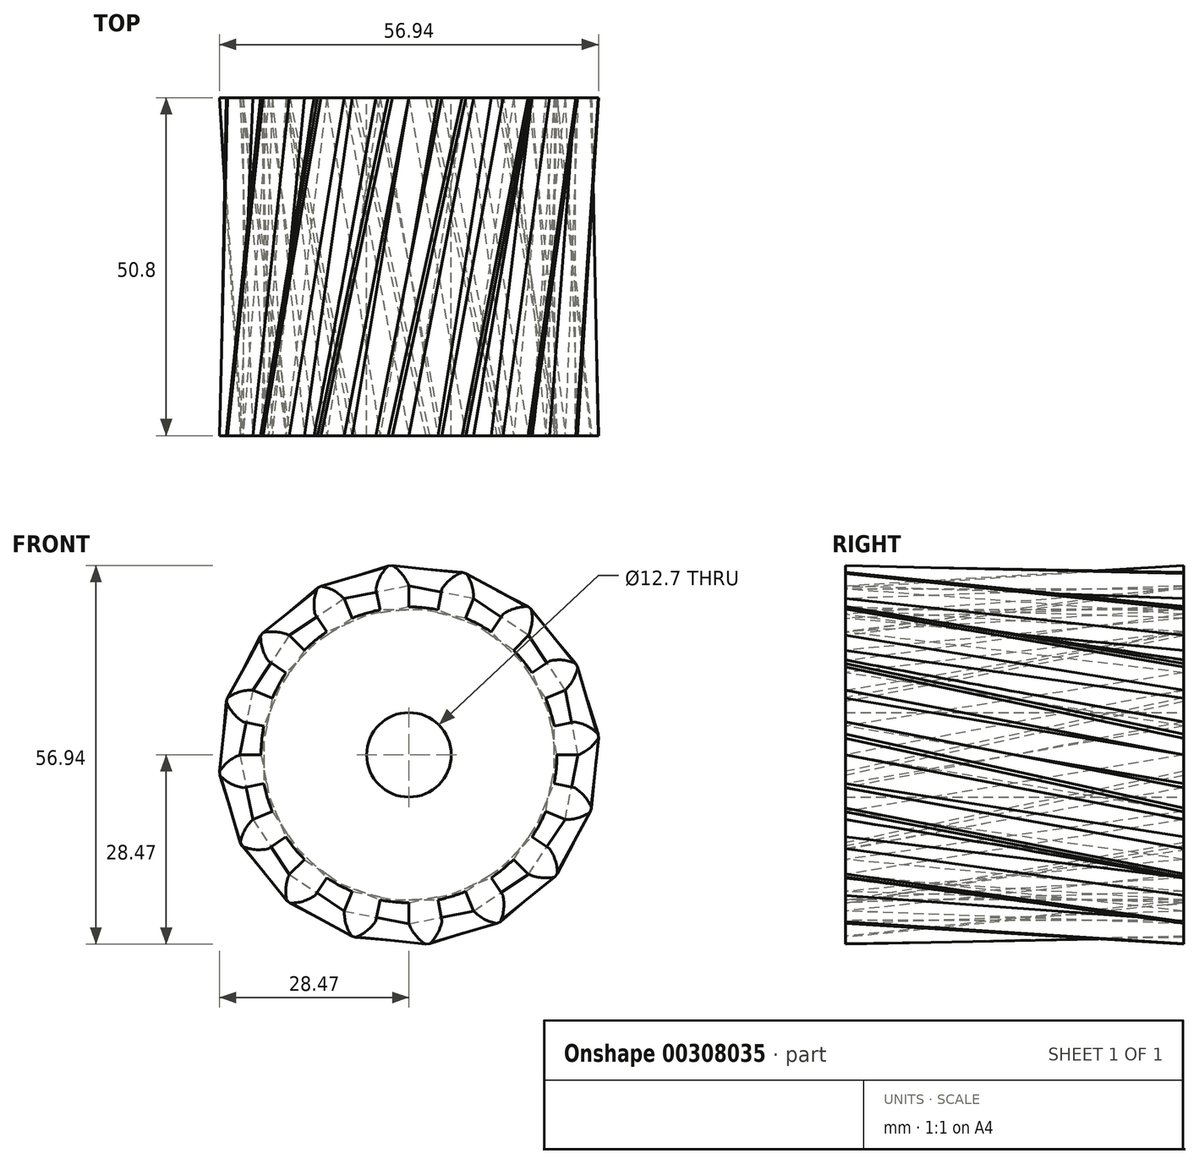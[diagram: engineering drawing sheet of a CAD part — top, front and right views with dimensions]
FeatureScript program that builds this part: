
annotation { "Feature Type Name" : "Feature", "Feature Type Description" : "" }
export const myFeature = defineFeature(function(context is Context, id is Id, definition is map)
    precondition{}
    {
        {
            var Q0;
            Q0=qCreatedBy(makeId("Front.planeOp"),FACE);
            var sketch = newSketch(context, id + "F0", { "sketchPlane" : qUnion([Q0])});
            skArc(sketch, "E0", {"start": v(-4.34, 21.8) * mm, "mid": v(-6.45, 21.27) * mm, "end": v(-8.5, 20.53) * mm});
            skArc(sketch, "E1.trimOffspring", {"start": v(0, 25.4) * mm, "mid": v(-1, 27.13) * mm, "end": v(-2.5, 28.47) * mm});
            skLineSegment(sketch, "E2", {"start": v(0, 25.4) * mm, "end": v(0, 22.23) * mm});
            skLineSegment(sketch, "E3", {"start": v(-2.5, 28.47) * mm, "end": v(-2.8, 28.44) * mm});
            skLineSegment(sketch, "E4.MirrorCS", {"start": v(-3.1, 28.4) * mm, "end": v(-2.8, 28.44) * mm});
            skArc(sketch, "E5.MirrorCS", {"start": v(-4.96, 24.91) * mm, "mid": v(-4.3, 26.8) * mm, "end": v(-3.1, 28.4) * mm});
            skLineSegment(sketch, "E6.MirrorCS", {"start": v(-4.96, 24.91) * mm, "end": v(-4.34, 21.8) * mm});
            skLineSegment(sketch, "E7.1.0", {"start": v(-14.11, 21.12) * mm, "end": v(-12.35, 18.48) * mm});
            skArc(sketch, "E7.1.1", {"start": v(-14.11, 21.12) * mm, "mid": v(-14.24, 23.12) * mm, "end": v(-13.74, 25.06) * mm});
            skLineSegment(sketch, "E7.1.2", {"start": v(-13.74, 25.06) * mm, "end": v(-13.47, 25.2) * mm});
            skLineSegment(sketch, "E7.1.3", {"start": v(-13.2, 25.34) * mm, "end": v(-13.47, 25.2) * mm});
            skArc(sketch, "E7.1.4", {"start": v(-9.72, 23.47) * mm, "mid": v(-11.31, 24.68) * mm, "end": v(-13.2, 25.34) * mm});
            skLineSegment(sketch, "E7.1.5", {"start": v(-9.72, 23.47) * mm, "end": v(-8.5, 20.53) * mm});
            skLineSegment(sketch, "E7.2.0", {"start": v(-21.12, 14.11) * mm, "end": v(-18.48, 12.35) * mm});
            skArc(sketch, "E7.2.1", {"start": v(-21.12, 14.11) * mm, "mid": v(-22, 15.9) * mm, "end": v(-22.28, 17.9) * mm});
            skLineSegment(sketch, "E7.2.2", {"start": v(-22.28, 17.9) * mm, "end": v(-22.09, 18.13) * mm});
            skLineSegment(sketch, "E7.2.3", {"start": v(-21.9, 18.36) * mm, "end": v(-22.09, 18.13) * mm});
            skArc(sketch, "E7.2.4", {"start": v(-17.96, 17.96) * mm, "mid": v(-19.9, 18.48) * mm, "end": v(-21.9, 18.36) * mm});
            skLineSegment(sketch, "E7.2.5", {"start": v(-17.96, 17.96) * mm, "end": v(-15.72, 15.72) * mm});
            skLineSegment(sketch, "E7.3.0", {"start": v(-24.91, 4.96) * mm, "end": v(-21.8, 4.34) * mm});
            skArc(sketch, "E7.3.1", {"start": v(-24.91, 4.96) * mm, "mid": v(-26.41, 6.28) * mm, "end": v(-27.43, 8) * mm});
            skLineSegment(sketch, "E7.3.2", {"start": v(-27.43, 8) * mm, "end": v(-27.34, 8.3) * mm});
            skLineSegment(sketch, "E7.3.3", {"start": v(-27.25, 8.59) * mm, "end": v(-27.34, 8.3) * mm});
            skArc(sketch, "E7.3.4", {"start": v(-23.47, 9.72) * mm, "mid": v(-25.45, 9.46) * mm, "end": v(-27.25, 8.59) * mm});
            skLineSegment(sketch, "E7.3.5", {"start": v(-23.47, 9.72) * mm, "end": v(-20.53, 8.5) * mm});
            skLineSegment(sketch, "E7.4.0", {"start": v(-24.91, -4.96) * mm, "end": v(-21.8, -4.34) * mm});
            skArc(sketch, "E7.4.1", {"start": v(-24.91, -4.96) * mm, "mid": v(-26.8, -4.3) * mm, "end": v(-28.4, -3.1) * mm});
            skLineSegment(sketch, "E7.4.2", {"start": v(-28.4, -3.1) * mm, "end": v(-28.44, -2.8) * mm});
            skLineSegment(sketch, "E7.4.3", {"start": v(-28.47, -2.5) * mm, "end": v(-28.44, -2.8) * mm});
            skArc(sketch, "E7.4.4", {"start": v(-25.4, 0) * mm, "mid": v(-27.13, -1) * mm, "end": v(-28.47, -2.5) * mm});
            skLineSegment(sketch, "E7.4.5", {"start": v(-25.4, 0) * mm, "end": v(-22.23, 0) * mm});
            skLineSegment(sketch, "E7.5.0", {"start": v(-21.12, -14.11) * mm, "end": v(-18.48, -12.35) * mm});
            skArc(sketch, "E7.5.1", {"start": v(-21.12, -14.11) * mm, "mid": v(-23.12, -14.24) * mm, "end": v(-25.06, -13.74) * mm});
            skLineSegment(sketch, "E7.5.2", {"start": v(-25.06, -13.74) * mm, "end": v(-25.2, -13.47) * mm});
            skLineSegment(sketch, "E7.5.3", {"start": v(-25.34, -13.2) * mm, "end": v(-25.2, -13.47) * mm});
            skArc(sketch, "E7.5.4", {"start": v(-23.47, -9.72) * mm, "mid": v(-24.68, -11.31) * mm, "end": v(-25.34, -13.2) * mm});
            skLineSegment(sketch, "E7.5.5", {"start": v(-23.47, -9.72) * mm, "end": v(-20.53, -8.5) * mm});
            skLineSegment(sketch, "E7.6.0", {"start": v(-14.11, -21.12) * mm, "end": v(-12.35, -18.48) * mm});
            skArc(sketch, "E7.6.1", {"start": v(-14.11, -21.12) * mm, "mid": v(-15.9, -22) * mm, "end": v(-17.9, -22.28) * mm});
            skLineSegment(sketch, "E7.6.2", {"start": v(-17.9, -22.28) * mm, "end": v(-18.13, -22.09) * mm});
            skLineSegment(sketch, "E7.6.3", {"start": v(-18.36, -21.9) * mm, "end": v(-18.13, -22.09) * mm});
            skArc(sketch, "E7.6.4", {"start": v(-17.96, -17.96) * mm, "mid": v(-18.48, -19.9) * mm, "end": v(-18.36, -21.9) * mm});
            skLineSegment(sketch, "E7.6.5", {"start": v(-17.96, -17.96) * mm, "end": v(-15.72, -15.72) * mm});
            skLineSegment(sketch, "E7.7.0", {"start": v(-4.96, -24.91) * mm, "end": v(-4.34, -21.8) * mm});
            skArc(sketch, "E7.7.1", {"start": v(-4.96, -24.91) * mm, "mid": v(-6.28, -26.41) * mm, "end": v(-8, -27.43) * mm});
            skLineSegment(sketch, "E7.7.2", {"start": v(-8, -27.43) * mm, "end": v(-8.3, -27.34) * mm});
            skLineSegment(sketch, "E7.7.3", {"start": v(-8.59, -27.25) * mm, "end": v(-8.3, -27.34) * mm});
            skArc(sketch, "E7.7.4", {"start": v(-9.72, -23.47) * mm, "mid": v(-9.46, -25.45) * mm, "end": v(-8.59, -27.25) * mm});
            skLineSegment(sketch, "E7.7.5", {"start": v(-9.72, -23.47) * mm, "end": v(-8.5, -20.53) * mm});
            skLineSegment(sketch, "E7.8.0", {"start": v(4.96, -24.91) * mm, "end": v(4.34, -21.8) * mm});
            skArc(sketch, "E7.8.1", {"start": v(4.96, -24.91) * mm, "mid": v(4.3, -26.8) * mm, "end": v(3.1, -28.4) * mm});
            skLineSegment(sketch, "E7.8.2", {"start": v(3.1, -28.4) * mm, "end": v(2.8, -28.44) * mm});
            skLineSegment(sketch, "E7.8.3", {"start": v(2.5, -28.47) * mm, "end": v(2.8, -28.44) * mm});
            skArc(sketch, "E7.8.4", {"start": v(0, -25.4) * mm, "mid": v(1, -27.13) * mm, "end": v(2.5, -28.47) * mm});
            skLineSegment(sketch, "E7.8.5", {"start": v(0, -25.4) * mm, "end": v(0, -22.23) * mm});
            skLineSegment(sketch, "E7.9.0", {"start": v(14.11, -21.12) * mm, "end": v(12.35, -18.48) * mm});
            skArc(sketch, "E7.9.1", {"start": v(14.11, -21.12) * mm, "mid": v(14.24, -23.12) * mm, "end": v(13.74, -25.06) * mm});
            skLineSegment(sketch, "E7.9.2", {"start": v(13.74, -25.06) * mm, "end": v(13.47, -25.2) * mm});
            skLineSegment(sketch, "E7.9.3", {"start": v(13.2, -25.34) * mm, "end": v(13.47, -25.2) * mm});
            skArc(sketch, "E7.9.4", {"start": v(9.72, -23.47) * mm, "mid": v(11.31, -24.68) * mm, "end": v(13.2, -25.34) * mm});
            skLineSegment(sketch, "E7.9.5", {"start": v(9.72, -23.47) * mm, "end": v(8.5, -20.53) * mm});
            skLineSegment(sketch, "E7.10.0", {"start": v(21.12, -14.11) * mm, "end": v(18.48, -12.35) * mm});
            skArc(sketch, "E7.10.1", {"start": v(21.12, -14.11) * mm, "mid": v(22, -15.9) * mm, "end": v(22.28, -17.9) * mm});
            skLineSegment(sketch, "E7.10.2", {"start": v(22.28, -17.9) * mm, "end": v(22.09, -18.13) * mm});
            skLineSegment(sketch, "E7.10.3", {"start": v(21.9, -18.36) * mm, "end": v(22.09, -18.13) * mm});
            skArc(sketch, "E7.10.4", {"start": v(17.96, -17.96) * mm, "mid": v(19.9, -18.48) * mm, "end": v(21.9, -18.36) * mm});
            skLineSegment(sketch, "E7.10.5", {"start": v(17.96, -17.96) * mm, "end": v(15.72, -15.72) * mm});
            skLineSegment(sketch, "E7.11.0", {"start": v(24.91, -4.96) * mm, "end": v(21.8, -4.34) * mm});
            skArc(sketch, "E7.11.1", {"start": v(24.91, -4.96) * mm, "mid": v(26.41, -6.28) * mm, "end": v(27.43, -8) * mm});
            skLineSegment(sketch, "E7.11.2", {"start": v(27.43, -8) * mm, "end": v(27.34, -8.3) * mm});
            skLineSegment(sketch, "E7.11.3", {"start": v(27.25, -8.59) * mm, "end": v(27.34, -8.3) * mm});
            skArc(sketch, "E7.11.4", {"start": v(23.47, -9.72) * mm, "mid": v(25.45, -9.46) * mm, "end": v(27.25, -8.59) * mm});
            skLineSegment(sketch, "E7.11.5", {"start": v(23.47, -9.72) * mm, "end": v(20.53, -8.5) * mm});
            skLineSegment(sketch, "E7.12.0", {"start": v(24.91, 4.96) * mm, "end": v(21.8, 4.34) * mm});
            skArc(sketch, "E7.12.1", {"start": v(24.91, 4.96) * mm, "mid": v(26.8, 4.3) * mm, "end": v(28.4, 3.1) * mm});
            skLineSegment(sketch, "E7.12.2", {"start": v(28.4, 3.1) * mm, "end": v(28.44, 2.8) * mm});
            skLineSegment(sketch, "E7.12.3", {"start": v(28.47, 2.5) * mm, "end": v(28.44, 2.8) * mm});
            skArc(sketch, "E7.12.4", {"start": v(25.4, 0) * mm, "mid": v(27.13, 1) * mm, "end": v(28.47, 2.5) * mm});
            skLineSegment(sketch, "E7.12.5", {"start": v(25.4, 0) * mm, "end": v(22.23, 0) * mm});
            skLineSegment(sketch, "E7.13.0", {"start": v(21.12, 14.11) * mm, "end": v(18.48, 12.35) * mm});
            skArc(sketch, "E7.13.1", {"start": v(21.12, 14.11) * mm, "mid": v(23.12, 14.24) * mm, "end": v(25.06, 13.74) * mm});
            skLineSegment(sketch, "E7.13.2", {"start": v(25.06, 13.74) * mm, "end": v(25.2, 13.47) * mm});
            skLineSegment(sketch, "E7.13.3", {"start": v(25.34, 13.2) * mm, "end": v(25.2, 13.47) * mm});
            skArc(sketch, "E7.13.4", {"start": v(23.47, 9.72) * mm, "mid": v(24.68, 11.31) * mm, "end": v(25.34, 13.2) * mm});
            skLineSegment(sketch, "E7.13.5", {"start": v(23.47, 9.72) * mm, "end": v(20.53, 8.5) * mm});
            skLineSegment(sketch, "E7.14.0", {"start": v(14.11, 21.12) * mm, "end": v(12.35, 18.48) * mm});
            skArc(sketch, "E7.14.1", {"start": v(14.11, 21.12) * mm, "mid": v(15.9, 22) * mm, "end": v(17.9, 22.28) * mm});
            skLineSegment(sketch, "E7.14.2", {"start": v(17.9, 22.28) * mm, "end": v(18.13, 22.09) * mm});
            skLineSegment(sketch, "E7.14.3", {"start": v(18.36, 21.9) * mm, "end": v(18.13, 22.09) * mm});
            skArc(sketch, "E7.14.4", {"start": v(17.96, 17.96) * mm, "mid": v(18.48, 19.9) * mm, "end": v(18.36, 21.9) * mm});
            skLineSegment(sketch, "E7.14.5", {"start": v(17.96, 17.96) * mm, "end": v(15.72, 15.72) * mm});
            skLineSegment(sketch, "E7.15.0", {"start": v(4.96, 24.91) * mm, "end": v(4.34, 21.8) * mm});
            skArc(sketch, "E7.15.1", {"start": v(4.96, 24.91) * mm, "mid": v(6.28, 26.41) * mm, "end": v(8, 27.43) * mm});
            skLineSegment(sketch, "E7.15.2", {"start": v(8, 27.43) * mm, "end": v(8.3, 27.34) * mm});
            skLineSegment(sketch, "E7.15.3", {"start": v(8.59, 27.25) * mm, "end": v(8.3, 27.34) * mm});
            skArc(sketch, "E7.15.4", {"start": v(9.72, 23.47) * mm, "mid": v(9.46, 25.45) * mm, "end": v(8.59, 27.25) * mm});
            skLineSegment(sketch, "E7.15.5", {"start": v(9.72, 23.47) * mm, "end": v(8.5, 20.53) * mm});
            skArc(sketch, "E8.trimOffspring", {"start": v(4.34, 21.8) * mm, "mid": v(2.18, 22.12) * mm, "end": v(0, 22.23) * mm});
            skArc(sketch, "E9.trimOffspring", {"start": v(-12.35, 18.48) * mm, "mid": v(-14.1, 17.18) * mm, "end": v(-15.72, 15.72) * mm});
            skArc(sketch, "E10.trimOffspring", {"start": v(12.35, 18.48) * mm, "mid": v(10.48, 19.6) * mm, "end": v(8.5, 20.53) * mm});
            skArc(sketch, "E11.trimOffspring", {"start": v(18.48, 12.35) * mm, "mid": v(17.18, 14.1) * mm, "end": v(15.72, 15.72) * mm});
            skArc(sketch, "E12.trimOffspring", {"start": v(21.8, 4.34) * mm, "mid": v(21.27, 6.45) * mm, "end": v(20.53, 8.5) * mm});
            skArc(sketch, "E13.trimOffspring", {"start": v(21.8, -4.34) * mm, "mid": v(22.12, -2.18) * mm, "end": v(22.23, 0) * mm});
            skArc(sketch, "E14.trimOffspring", {"start": v(18.48, -12.35) * mm, "mid": v(19.6, -10.48) * mm, "end": v(20.53, -8.5) * mm});
            skArc(sketch, "E15.trimOffspring", {"start": v(12.35, -18.48) * mm, "mid": v(14.1, -17.18) * mm, "end": v(15.72, -15.72) * mm});
            skArc(sketch, "E16.trimOffspring", {"start": v(4.34, -21.8) * mm, "mid": v(6.45, -21.27) * mm, "end": v(8.5, -20.53) * mm});
            skArc(sketch, "E17.trimOffspring", {"start": v(-4.34, -21.8) * mm, "mid": v(-2.18, -22.12) * mm, "end": v(0, -22.23) * mm});
            skArc(sketch, "E18.trimOffspring", {"start": v(-12.35, -18.48) * mm, "mid": v(-10.48, -19.6) * mm, "end": v(-8.5, -20.53) * mm});
            skArc(sketch, "E19.trimOffspring", {"start": v(-18.48, -12.35) * mm, "mid": v(-17.18, -14.1) * mm, "end": v(-15.72, -15.72) * mm});
            skArc(sketch, "E20.trimOffspring", {"start": v(-21.8, -4.34) * mm, "mid": v(-21.27, -6.45) * mm, "end": v(-20.53, -8.5) * mm});
            skArc(sketch, "E21.trimOffspring", {"start": v(-21.8, 4.34) * mm, "mid": v(-22.12, 2.18) * mm, "end": v(-22.23, 0) * mm});
            skArc(sketch, "E22.trimOffspring", {"start": v(-18.48, 12.35) * mm, "mid": v(-19.6, 10.48) * mm, "end": v(-20.53, 8.5) * mm});
            skSolve(sketch);
        }
        {
            var Q0;
            Q0=makeQuery(id+"F0.imprint","IMPRINT",FACE,{"disambiguationData":[TD([[makeQuery(id+"F0.imprint","IMPRINT",EDGE,{"derivedFrom":sQuery(id+"F0.wireOp",EDGE,"E0")}),1.0]])]});
            cPlane(context, id + "F1", {"entities" : qUnion([Q0]), "cplaneType" : CPlaneType.OFFSET, "offset" : 50.8 * mm, "width" : 152.4 * mm, "height" : 152.4 * mm});
        }
        {
            var Q0;
            Q0=qCreatedBy(id+"F1.planeOp",FACE);
            var sketch = newSketch(context, id + "F2", { "sketchPlane" : qUnion([Q0])});
            skArc(sketch, "E23.0.0", {"start": v(-27.43, 8) * mm, "mid": v(-26.41, 6.28) * mm, "end": v(-24.91, 4.96) * mm});
            skLineSegment(sketch, "E23.0.1", {"start": v(-24.91, 4.96) * mm, "end": v(-21.8, 4.34) * mm});
            skArc(sketch, "E23.0.2", {"start": v(-21.8, 4.34) * mm, "mid": v(-22.12, 2.18) * mm, "end": v(-22.23, 0) * mm});
            skLineSegment(sketch, "E23.0.3", {"start": v(-22.23, 0) * mm, "end": v(-25.4, 0) * mm});
            skArc(sketch, "E23.0.4", {"start": v(-25.4, 0) * mm, "mid": v(-27.13, -1) * mm, "end": v(-28.47, -2.5) * mm});
            skLineSegment(sketch, "E23.0.5", {"start": v(-28.47, -2.5) * mm, "end": v(-28.44, -2.8) * mm});
            skLineSegment(sketch, "E23.0.6", {"start": v(-28.44, -2.8) * mm, "end": v(-28.4, -3.1) * mm});
            skArc(sketch, "E23.0.7", {"start": v(-28.4, -3.1) * mm, "mid": v(-26.8, -4.3) * mm, "end": v(-24.91, -4.96) * mm});
            skLineSegment(sketch, "E23.0.8", {"start": v(-24.91, -4.96) * mm, "end": v(-21.8, -4.34) * mm});
            skArc(sketch, "E23.0.9", {"start": v(-21.8, -4.34) * mm, "mid": v(-21.27, -6.45) * mm, "end": v(-20.53, -8.5) * mm});
            skLineSegment(sketch, "E23.0.10", {"start": v(-20.53, -8.5) * mm, "end": v(-23.47, -9.72) * mm});
            skArc(sketch, "E23.0.11", {"start": v(-23.47, -9.72) * mm, "mid": v(-24.68, -11.31) * mm, "end": v(-25.34, -13.2) * mm});
            skLineSegment(sketch, "E23.0.12", {"start": v(-25.34, -13.2) * mm, "end": v(-25.2, -13.47) * mm});
            skLineSegment(sketch, "E23.0.13", {"start": v(-25.2, -13.47) * mm, "end": v(-25.06, -13.74) * mm});
            skArc(sketch, "E23.0.14", {"start": v(-25.06, -13.74) * mm, "mid": v(-23.12, -14.24) * mm, "end": v(-21.12, -14.11) * mm});
            skLineSegment(sketch, "E23.0.15", {"start": v(-21.12, -14.11) * mm, "end": v(-18.48, -12.35) * mm});
            skArc(sketch, "E23.0.16", {"start": v(-18.48, -12.35) * mm, "mid": v(-17.18, -14.1) * mm, "end": v(-15.72, -15.72) * mm});
            skLineSegment(sketch, "E23.0.17", {"start": v(-15.72, -15.72) * mm, "end": v(-17.96, -17.96) * mm});
            skArc(sketch, "E23.0.18", {"start": v(-17.96, -17.96) * mm, "mid": v(-18.48, -19.9) * mm, "end": v(-18.36, -21.9) * mm});
            skLineSegment(sketch, "E23.0.19", {"start": v(-18.36, -21.9) * mm, "end": v(-18.13, -22.09) * mm});
            skLineSegment(sketch, "E23.0.20", {"start": v(-18.13, -22.09) * mm, "end": v(-17.9, -22.28) * mm});
            skArc(sketch, "E23.0.21", {"start": v(-17.9, -22.28) * mm, "mid": v(-15.9, -22) * mm, "end": v(-14.11, -21.12) * mm});
            skLineSegment(sketch, "E23.0.22", {"start": v(-14.11, -21.12) * mm, "end": v(-12.35, -18.48) * mm});
            skArc(sketch, "E23.0.23", {"start": v(-12.35, -18.48) * mm, "mid": v(-10.48, -19.6) * mm, "end": v(-8.5, -20.53) * mm});
            skLineSegment(sketch, "E23.0.24", {"start": v(-8.5, -20.53) * mm, "end": v(-9.72, -23.47) * mm});
            skArc(sketch, "E23.0.25", {"start": v(-9.72, -23.47) * mm, "mid": v(-9.46, -25.45) * mm, "end": v(-8.59, -27.25) * mm});
            skLineSegment(sketch, "E23.0.26", {"start": v(-8.59, -27.25) * mm, "end": v(-8.3, -27.34) * mm});
            skLineSegment(sketch, "E23.0.27", {"start": v(-8.3, -27.34) * mm, "end": v(-8, -27.43) * mm});
            skArc(sketch, "E23.0.28", {"start": v(-8, -27.43) * mm, "mid": v(-6.28, -26.41) * mm, "end": v(-4.96, -24.91) * mm});
            skLineSegment(sketch, "E23.0.29", {"start": v(-4.96, -24.91) * mm, "end": v(-4.34, -21.8) * mm});
            skArc(sketch, "E23.0.30", {"start": v(-4.34, -21.8) * mm, "mid": v(-2.18, -22.12) * mm, "end": v(0, -22.23) * mm});
            skLineSegment(sketch, "E23.0.31", {"start": v(0, -22.23) * mm, "end": v(0, -25.4) * mm});
            skArc(sketch, "E23.0.32", {"start": v(0, -25.4) * mm, "mid": v(1, -27.13) * mm, "end": v(2.5, -28.47) * mm});
            skLineSegment(sketch, "E23.0.33", {"start": v(2.5, -28.47) * mm, "end": v(2.8, -28.44) * mm});
            skLineSegment(sketch, "E23.0.34", {"start": v(2.8, -28.44) * mm, "end": v(3.1, -28.4) * mm});
            skArc(sketch, "E23.0.35", {"start": v(3.1, -28.4) * mm, "mid": v(4.3, -26.8) * mm, "end": v(4.96, -24.91) * mm});
            skLineSegment(sketch, "E23.0.36", {"start": v(4.96, -24.91) * mm, "end": v(4.34, -21.8) * mm});
            skArc(sketch, "E23.0.37", {"start": v(4.34, -21.8) * mm, "mid": v(6.45, -21.27) * mm, "end": v(8.5, -20.53) * mm});
            skLineSegment(sketch, "E23.0.38", {"start": v(8.5, -20.53) * mm, "end": v(9.72, -23.47) * mm});
            skArc(sketch, "E23.0.39", {"start": v(9.72, -23.47) * mm, "mid": v(11.31, -24.68) * mm, "end": v(13.2, -25.34) * mm});
            skLineSegment(sketch, "E23.0.40", {"start": v(13.2, -25.34) * mm, "end": v(13.47, -25.2) * mm});
            skLineSegment(sketch, "E23.0.41", {"start": v(13.47, -25.2) * mm, "end": v(13.74, -25.06) * mm});
            skArc(sketch, "E23.0.42", {"start": v(13.74, -25.06) * mm, "mid": v(14.24, -23.12) * mm, "end": v(14.11, -21.12) * mm});
            skLineSegment(sketch, "E23.0.43", {"start": v(14.11, -21.12) * mm, "end": v(12.35, -18.48) * mm});
            skArc(sketch, "E23.0.44", {"start": v(12.35, -18.48) * mm, "mid": v(14.1, -17.18) * mm, "end": v(15.72, -15.72) * mm});
            skLineSegment(sketch, "E23.0.45", {"start": v(15.72, -15.72) * mm, "end": v(17.96, -17.96) * mm});
            skArc(sketch, "E23.0.46", {"start": v(17.96, -17.96) * mm, "mid": v(19.9, -18.48) * mm, "end": v(21.9, -18.36) * mm});
            skLineSegment(sketch, "E23.0.47", {"start": v(21.9, -18.36) * mm, "end": v(22.09, -18.13) * mm});
            skLineSegment(sketch, "E23.0.48", {"start": v(22.09, -18.13) * mm, "end": v(22.28, -17.9) * mm});
            skArc(sketch, "E23.0.49", {"start": v(22.28, -17.9) * mm, "mid": v(22, -15.9) * mm, "end": v(21.12, -14.11) * mm});
            skLineSegment(sketch, "E23.0.50", {"start": v(21.12, -14.11) * mm, "end": v(18.48, -12.35) * mm});
            skArc(sketch, "E23.0.51", {"start": v(18.48, -12.35) * mm, "mid": v(19.6, -10.48) * mm, "end": v(20.53, -8.5) * mm});
            skLineSegment(sketch, "E23.0.52", {"start": v(20.53, -8.5) * mm, "end": v(23.47, -9.72) * mm});
            skArc(sketch, "E23.0.53", {"start": v(23.47, -9.72) * mm, "mid": v(25.45, -9.46) * mm, "end": v(27.25, -8.59) * mm});
            skLineSegment(sketch, "E23.0.54", {"start": v(27.25, -8.59) * mm, "end": v(27.34, -8.3) * mm});
            skLineSegment(sketch, "E23.0.55", {"start": v(27.34, -8.3) * mm, "end": v(27.43, -8) * mm});
            skArc(sketch, "E23.0.56", {"start": v(27.43, -8) * mm, "mid": v(26.41, -6.28) * mm, "end": v(24.91, -4.96) * mm});
            skLineSegment(sketch, "E23.0.57", {"start": v(24.91, -4.96) * mm, "end": v(21.8, -4.34) * mm});
            skArc(sketch, "E23.0.58", {"start": v(21.8, -4.34) * mm, "mid": v(22.12, -2.18) * mm, "end": v(22.23, 0) * mm});
            skLineSegment(sketch, "E23.0.59", {"start": v(22.23, 0) * mm, "end": v(25.4, 0) * mm});
            skArc(sketch, "E23.0.60", {"start": v(25.4, 0) * mm, "mid": v(27.13, 1) * mm, "end": v(28.47, 2.5) * mm});
            skLineSegment(sketch, "E23.0.61", {"start": v(28.47, 2.5) * mm, "end": v(28.44, 2.8) * mm});
            skLineSegment(sketch, "E23.0.62", {"start": v(28.44, 2.8) * mm, "end": v(28.4, 3.1) * mm});
            skArc(sketch, "E23.0.63", {"start": v(28.4, 3.1) * mm, "mid": v(26.8, 4.3) * mm, "end": v(24.91, 4.96) * mm});
            skLineSegment(sketch, "E23.0.64", {"start": v(24.91, 4.96) * mm, "end": v(21.8, 4.34) * mm});
            skArc(sketch, "E23.0.65", {"start": v(21.8, 4.34) * mm, "mid": v(21.27, 6.45) * mm, "end": v(20.53, 8.5) * mm});
            skLineSegment(sketch, "E23.0.66", {"start": v(20.53, 8.5) * mm, "end": v(23.47, 9.72) * mm});
            skArc(sketch, "E23.0.67", {"start": v(23.47, 9.72) * mm, "mid": v(24.68, 11.31) * mm, "end": v(25.34, 13.2) * mm});
            skLineSegment(sketch, "E23.0.68", {"start": v(25.34, 13.2) * mm, "end": v(25.2, 13.47) * mm});
            skLineSegment(sketch, "E23.0.69", {"start": v(25.2, 13.47) * mm, "end": v(25.06, 13.74) * mm});
            skArc(sketch, "E23.0.70", {"start": v(25.06, 13.74) * mm, "mid": v(23.12, 14.24) * mm, "end": v(21.12, 14.11) * mm});
            skLineSegment(sketch, "E23.0.71", {"start": v(21.12, 14.11) * mm, "end": v(18.48, 12.35) * mm});
            skArc(sketch, "E23.0.72", {"start": v(18.48, 12.35) * mm, "mid": v(17.18, 14.1) * mm, "end": v(15.72, 15.72) * mm});
            skLineSegment(sketch, "E23.0.73", {"start": v(15.72, 15.72) * mm, "end": v(17.96, 17.96) * mm});
            skArc(sketch, "E23.0.74", {"start": v(17.96, 17.96) * mm, "mid": v(18.48, 19.9) * mm, "end": v(18.36, 21.9) * mm});
            skLineSegment(sketch, "E23.0.75", {"start": v(18.36, 21.9) * mm, "end": v(18.13, 22.09) * mm});
            skLineSegment(sketch, "E23.0.76", {"start": v(18.13, 22.09) * mm, "end": v(17.9, 22.28) * mm});
            skArc(sketch, "E23.0.77", {"start": v(17.9, 22.28) * mm, "mid": v(15.9, 22) * mm, "end": v(14.11, 21.12) * mm});
            skLineSegment(sketch, "E23.0.78", {"start": v(14.11, 21.12) * mm, "end": v(12.35, 18.48) * mm});
            skArc(sketch, "E23.0.79", {"start": v(12.35, 18.48) * mm, "mid": v(10.48, 19.6) * mm, "end": v(8.5, 20.53) * mm});
            skLineSegment(sketch, "E23.0.80", {"start": v(8.5, 20.53) * mm, "end": v(9.72, 23.47) * mm});
            skArc(sketch, "E23.0.81", {"start": v(9.72, 23.47) * mm, "mid": v(9.46, 25.45) * mm, "end": v(8.59, 27.25) * mm});
            skLineSegment(sketch, "E23.0.82", {"start": v(8.59, 27.25) * mm, "end": v(8.3, 27.34) * mm});
            skLineSegment(sketch, "E23.0.83", {"start": v(8.3, 27.34) * mm, "end": v(8, 27.43) * mm});
            skArc(sketch, "E23.0.84", {"start": v(8, 27.43) * mm, "mid": v(6.28, 26.41) * mm, "end": v(4.96, 24.91) * mm});
            skLineSegment(sketch, "E23.0.85", {"start": v(4.96, 24.91) * mm, "end": v(4.34, 21.8) * mm});
            skArc(sketch, "E23.0.86", {"start": v(4.34, 21.8) * mm, "mid": v(2.18, 22.12) * mm, "end": v(0, 22.23) * mm});
            skLineSegment(sketch, "E23.0.87", {"start": v(0, 22.23) * mm, "end": v(0, 25.4) * mm});
            skArc(sketch, "E23.0.88", {"start": v(0, 25.4) * mm, "mid": v(-1, 27.13) * mm, "end": v(-2.5, 28.47) * mm});
            skLineSegment(sketch, "E23.0.89", {"start": v(-2.5, 28.47) * mm, "end": v(-2.8, 28.44) * mm});
            skLineSegment(sketch, "E23.0.90", {"start": v(-2.8, 28.44) * mm, "end": v(-3.1, 28.4) * mm});
            skArc(sketch, "E23.0.91", {"start": v(-3.1, 28.4) * mm, "mid": v(-4.3, 26.8) * mm, "end": v(-4.96, 24.91) * mm});
            skLineSegment(sketch, "E23.0.92", {"start": v(-4.96, 24.91) * mm, "end": v(-4.34, 21.8) * mm});
            skArc(sketch, "E23.0.93", {"start": v(-4.34, 21.8) * mm, "mid": v(-6.45, 21.27) * mm, "end": v(-8.5, 20.53) * mm});
            skLineSegment(sketch, "E23.0.94", {"start": v(-8.5, 20.53) * mm, "end": v(-9.72, 23.47) * mm});
            skArc(sketch, "E23.0.95", {"start": v(-9.72, 23.47) * mm, "mid": v(-11.31, 24.68) * mm, "end": v(-13.2, 25.34) * mm});
            skLineSegment(sketch, "E23.0.96", {"start": v(-13.2, 25.34) * mm, "end": v(-13.47, 25.2) * mm});
            skLineSegment(sketch, "E23.0.97", {"start": v(-13.47, 25.2) * mm, "end": v(-13.74, 25.06) * mm});
            skArc(sketch, "E23.0.98", {"start": v(-13.74, 25.06) * mm, "mid": v(-14.24, 23.12) * mm, "end": v(-14.11, 21.12) * mm});
            skLineSegment(sketch, "E23.0.99", {"start": v(-14.11, 21.12) * mm, "end": v(-12.35, 18.48) * mm});
            skArc(sketch, "E23.0.100", {"start": v(-12.35, 18.48) * mm, "mid": v(-14.1, 17.18) * mm, "end": v(-15.72, 15.72) * mm});
            skLineSegment(sketch, "E23.0.101", {"start": v(-15.72, 15.72) * mm, "end": v(-17.96, 17.96) * mm});
            skArc(sketch, "E23.0.102", {"start": v(-17.96, 17.96) * mm, "mid": v(-19.9, 18.48) * mm, "end": v(-21.9, 18.36) * mm});
            skLineSegment(sketch, "E23.0.103", {"start": v(-21.9, 18.36) * mm, "end": v(-22.09, 18.13) * mm});
            skLineSegment(sketch, "E23.0.104", {"start": v(-22.09, 18.13) * mm, "end": v(-22.28, 17.9) * mm});
            skArc(sketch, "E23.0.105", {"start": v(-22.28, 17.9) * mm, "mid": v(-22, 15.9) * mm, "end": v(-21.12, 14.11) * mm});
            skLineSegment(sketch, "E23.0.106", {"start": v(-21.12, 14.11) * mm, "end": v(-18.48, 12.35) * mm});
            skArc(sketch, "E23.0.107", {"start": v(-18.48, 12.35) * mm, "mid": v(-19.6, 10.48) * mm, "end": v(-20.53, 8.5) * mm});
            skLineSegment(sketch, "E23.0.108", {"start": v(-20.53, 8.5) * mm, "end": v(-23.47, 9.72) * mm});
            skArc(sketch, "E23.0.109", {"start": v(-23.47, 9.72) * mm, "mid": v(-25.45, 9.46) * mm, "end": v(-27.25, 8.59) * mm});
            skLineSegment(sketch, "E23.0.110", {"start": v(-27.25, 8.59) * mm, "end": v(-27.34, 8.3) * mm});
            skLineSegment(sketch, "E23.0.111", {"start": v(-27.34, 8.3) * mm, "end": v(-27.43, 8) * mm});
            skSolve(sketch);
        }
        {
            var Q0;
            Q0=makeQuery(id+"F0.imprint","IMPRINT",FACE,{"disambiguationData":[TD([[makeQuery(id+"F0.imprint","IMPRINT",EDGE,{"derivedFrom":sQuery(id+"F0.wireOp",EDGE,"E0")}),1.0]])]});
            var Q1;
            Q1=makeQuery(id+"F2.imprint","IMPRINT",FACE,{"disambiguationData":[TD([[makeQuery(id+"F2.imprint","IMPRINT",EDGE,{"derivedFrom":sQuery(id+"F2.wireOp",EDGE,"E23.0.0")}),1.0]])]});
            var Q2;
            Q2=sQuery(id+"F2.wireOp",VERTEX,"E23.0.93.start");
            var Q3;
            Q3=sQuery(id+"F0.wireOp",VERTEX,"E8.trimOffspring.start");
            loft(context, id + "F3", {"sheetProfilesArray" : [{ "sheetProfileEntities" : qUnion([Q0]) }, { "sheetProfileEntities" : qUnion([Q1]) }], "matchConnections" : true, "connections" : [{ "connectionEntities" : qUnion([Q2, Q3]), "connectionEdgeQueries" : qUnion([]), "connectionEdgeParameters" : [] }]});
        }
        {
            var Q0;
            Q0=makeQuery(id+"F3.opLoft","CAP_FACE",FACE,{"disambiguationData":[OSD([makeQuery(id+"F0.imprint","IMPRINT",FACE,{"disambiguationData":[TD([[makeQuery(id+"F0.imprint","IMPRINT",EDGE,{"derivedFrom":sQuery(id+"F0.wireOp",EDGE,"E0")}),1.0]])]})])],"isStart":true});
            var sketch = newSketch(context, id + "F4", { "sketchPlane" : qUnion([Q0])});
            skCircle(sketch, "E24", {"center": v(0, 0) * mm, "radius": 6.35 * mm});
            skSolve(sketch);
        }
        {
            var Q0;
            Q0=makeQuery(id+"F4.imprint","IMPRINT",FACE,{"disambiguationData":[TD([[makeQuery(id+"F4.imprint","IMPRINT",EDGE,{"derivedFrom":sQuery(id+"F4.wireOp",EDGE,"E24")}),1.0]])]});
            extrude(context, id + "F5", {"entities" : qUnion([Q0]), "operationType" : NewBodyOperationType.REMOVE, "endBound" : BoundingType.THROUGH_ALL, "oppositeDirection" : true, "depth" : 25.4 * mm});
        }
    });
